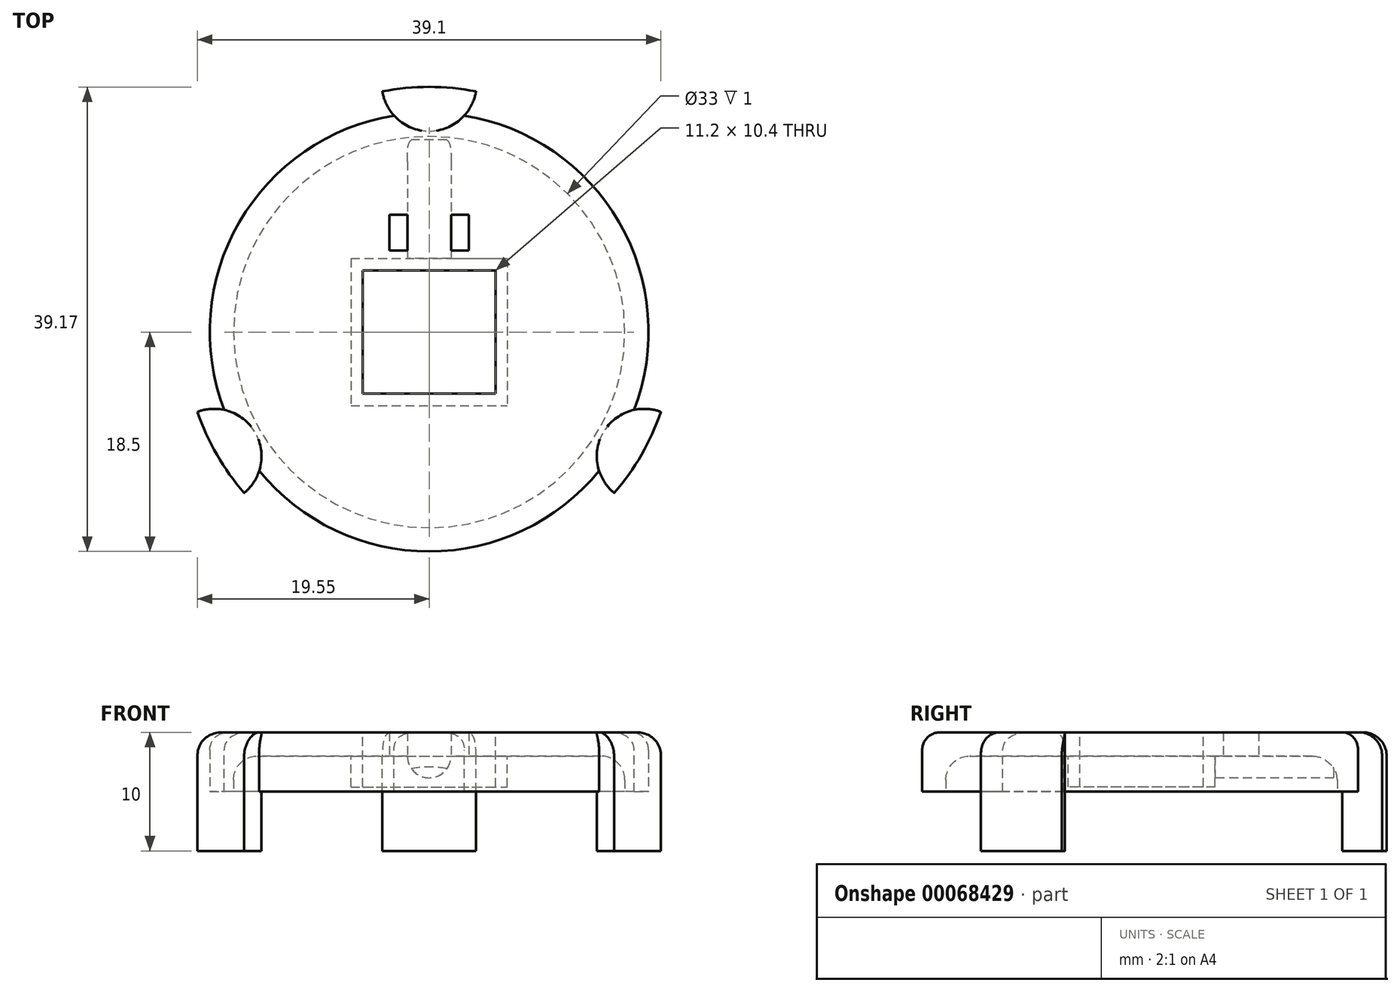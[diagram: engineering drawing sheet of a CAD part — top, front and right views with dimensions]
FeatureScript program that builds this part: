
annotation { "Feature Type Name" : "Feature", "Feature Type Description" : "" }
export const myFeature = defineFeature(function(context is Context, id is Id, definition is map)
    precondition{}
    {
        {
            var Q0;
            Q0=qCreatedBy(makeId("Top.planeOp"),FACE);
            var sketch = newSketch(context, id + "F0", { "sketchPlane" : qUnion([Q0])});
            skCircle(sketch, "E0", {"center": v(0, 0) * mm, "radius": 18.5 * mm});
            skCircle(sketch, "E1", {"center": v(0, 0) * mm, "radius": 20.88 * mm, "construction": true});
            skCircle(sketch, "E2", {"center": v(0, 0) * mm, "radius": 19.1 * mm, "construction": true});
            skCircle(sketch, "E3", {"center": v(-20.88, 0) * mm, "radius": 3.64 * mm});
            skCircle(sketch, "E4", {"center": v(10.44, 18.09) * mm, "radius": 3.64 * mm});
            skCircle(sketch, "E5", {"center": v(10.44, -18.09) * mm, "radius": 3.64 * mm});
            skLineSegment(sketch, "E6", {"start": v(-20.88, 0) * mm, "end": v(0, 0) * mm, "construction": true});
            skLineSegment(sketch, "E7", {"start": v(0, 0) * mm, "end": v(10.44, -18.09) * mm, "construction": true});
            skLineSegment(sketch, "E8", {"start": v(0, 0) * mm, "end": v(10.44, 18.09) * mm, "construction": true});
            skSolve(sketch);
        }
        {
            var Q0;
            {var subQ0=sQuery(id+"F0.wireOp",EDGE,"E4");var subQ1=sQuery(id+"F0.wireOp",EDGE,"E0");var subQ2=makeQuery(id+"F0.imprint","INTERSECT",VERTEX,{"disambiguationData":[OD(0.0)],"derivedFrom":[subQ1,subQ0]});Q0=makeQuery(id+"F0.imprint","IMPRINT",FACE,{"disambiguationData":[TD([[makeQuery(id+"F0.imprint","IMPRINT",EDGE,{"disambiguationData":[TD([[subQ2,1.0]])],"derivedFrom":subQ1}),1.0]])]});}
            var Q1;
            {var subQ0=sQuery(id+"F0.wireOp",EDGE,"E3");var subQ1=sQuery(id+"F0.wireOp",EDGE,"E0");var subQ2=makeQuery(id+"F0.imprint","INTERSECT",VERTEX,{"disambiguationData":[OD(0.0)],"derivedFrom":[subQ1,subQ0]});Q1=makeQuery(id+"F0.imprint","IMPRINT",FACE,{"disambiguationData":[TD([[makeQuery(id+"F0.imprint","IMPRINT",EDGE,{"disambiguationData":[TD([[subQ2,-1.0]])],"derivedFrom":subQ1}),1.0]])]});}
            var Q2;
            {var subQ0=sQuery(id+"F0.wireOp",EDGE,"E5");var subQ1=sQuery(id+"F0.wireOp",EDGE,"E0");var subQ2=makeQuery(id+"F0.imprint","INTERSECT",VERTEX,{"disambiguationData":[OD(0.0)],"derivedFrom":[subQ1,subQ0]});Q2=makeQuery(id+"F0.imprint","IMPRINT",FACE,{"disambiguationData":[TD([[makeQuery(id+"F0.imprint","IMPRINT",EDGE,{"disambiguationData":[TD([[subQ2,-1.0]])],"derivedFrom":subQ1}),1.0]])]});}
            var Q3;
            {var subQ1=sQuery(id+"F0.wireOp",EDGE,"E0");var subQ4=sQuery(id+"F0.wireOp",EDGE,"E4");var subQ9=makeQuery(id+"F0.imprint","INTERSECT",VERTEX,{"disambiguationData":[OD(0.0)],"derivedFrom":[subQ1,subQ4]});Q3=makeQuery(id+"F0.imprint","IMPRINT",FACE,{"disambiguationData":[TD([[makeQuery(id+"F0.imprint","IMPRINT",EDGE,{"disambiguationData":[TD([[subQ9,-1.0]])],"derivedFrom":subQ1}),1.0]])]});}
            extrude(context, id + "F1", {"entities" : qUnion([Q0, Q1, Q2, Q3]), "depth" : 5 * mm});
        }
        {
            var Q0;
            Q0=makeQuery(id+"F1.opExtrude","CAP_FACE",FACE,{"disambiguationData":[OSD([sQuery(id+"F0.wireOp",EDGE,"E0")])],"isStart":true});
            var Q1;
            Q1=makeQuery(id+"F1.opExtrude","SWEPT_BODY",BODY,{"disambiguationData":[OSD([sQuery(id+"F0.wireOp",EDGE,"E0")])]});
            shell(context, id + "F2", {"entities" : qUnion([Q0]), "parts" : qUnion([Q1]), "thickness" : 2 * mm});
        }
        {
            var Q0;
            {var subQ0=sQuery(id+"F0.wireOp",EDGE,"E0");Q0=makeQuery(id+"F2.opShell","OFFSET_EDGE",EDGE,{"disambiguationData":[OSD([subQ0]),TDD([makeQuery(id+"F1.opExtrude","CAP_EDGE",EDGE,{"disambiguationData":[OSD([subQ0])],"isStart":false})])]});}
            fillet(context, id + "F3", {"entities" : qUnion([Q0]), "radius" : 2 * mm, "tangentPropagation" : true, "allowEdgeOverflow" : false});
        }
        {
            var Q0;
            Q0=makeQuery(id+"F1.opExtrude","CAP_FACE",FACE,{"disambiguationData":[OSD([sQuery(id+"F0.wireOp",EDGE,"E0")])],"isStart":false});
            var sketch = newSketch(context, id + "F4", { "sketchPlane" : qUnion([Q0])});
            skLineSegment(sketch, "E9.rect.bottom", {"start": v(-5.6, 5.2) * mm, "end": v(5.6, 5.2) * mm});
            skLineSegment(sketch, "E9.rect.top", {"start": v(-5.6, -5.2) * mm, "end": v(5.6, -5.2) * mm});
            skLineSegment(sketch, "E9.rect.left", {"start": v(-5.6, 5.2) * mm, "end": v(-5.6, -5.2) * mm});
            skLineSegment(sketch, "E9.rect.right", {"start": v(5.6, 5.2) * mm, "end": v(5.6, -5.2) * mm});
            skPoint(sketch, "E9.rect.middle", {"position": v(0, 0) * mm});
            skLineSegment(sketch, "E10.0", {"start": v(-6.6, 6.2) * mm, "end": v(-6.6, -6.2) * mm});
            skLineSegment(sketch, "E10.1", {"start": v(-6.6, 6.2) * mm, "end": v(6.6, 6.2) * mm});
            skLineSegment(sketch, "E10.2", {"start": v(6.6, 6.2) * mm, "end": v(6.6, -6.2) * mm});
            skLineSegment(sketch, "E10.3", {"start": v(-6.6, -6.2) * mm, "end": v(6.6, -6.2) * mm});
            skSolve(sketch);
        }
        {
            var Q0;
            Q0=makeQuery(id+"F4.imprint","IMPRINT",FACE,{"disambiguationData":[TD([[makeQuery(id+"F4.imprint","IMPRINT",EDGE,{"derivedFrom":sQuery(id+"F4.wireOp",EDGE,"E9.rect.bottom")}),-1.0]])]});
            extrude(context, id + "F5", {"entities" : qUnion([Q0]), "operationType" : NewBodyOperationType.REMOVE, "oppositeDirection" : true, "depth" : 25 * mm});
        }
        {
            var Q0;
            Q0=makeQuery(id+"F4.imprint","IMPRINT",FACE,{"disambiguationData":[TD([[makeQuery(id+"F4.imprint","IMPRINT",EDGE,{"derivedFrom":sQuery(id+"F4.wireOp",EDGE,"E9.rect.bottom")}),1.0]])]});
            extrude(context, id + "F6", {"entities" : qUnion([Q0]), "operationType" : NewBodyOperationType.ADD, "oppositeDirection" : true, "depth" : 4.6 * mm});
        }
        {
            var Q0;
            Q0=makeQuery(id+"F6.opExtrude","SWEPT_FACE",FACE,{"disambiguationData":[OSD([sQuery(id+"F4.wireOp",EDGE,"E10.1")])]});
            var sketch = newSketch(context, id + "F7", { "sketchPlane" : qUnion([Q0])});
            skArc(sketch, "E11", {"start": v(-1.84, 3) * mm, "mid": v(0, 1.16) * mm, "end": v(1.84, 3) * mm});
            skSolve(sketch);
        }
        {
            var Q0;
            {var subQ0=sQuery(id+"F7.wireOp",EDGE,"E11");Q0=makeQuery(id+"F7.imprint","IMPRINT",FACE,{"disambiguationData":[TD([[makeQuery(id+"F7.imprint","IMPRINT",EDGE,{"derivedFrom":subQ0}),1.0]])]});}
            extrude(context, id + "F8", {"entities" : qUnion([Q0]), "operationType" : NewBodyOperationType.ADD, "depth" : 10 * mm});
        }
        {
            var Q0;
            {var subQ0=sQuery(id+"F0.wireOp",EDGE,"E0");Q0=makeQuery(id+"F2.opShell","OFFSET_FACE",FACE,{"disambiguationData":[OSD([subQ0]),TDD([makeQuery(id+"F1.opExtrude","CAP_FACE",FACE,{"disambiguationData":[OSD([subQ0])],"isStart":false})])]});}
            var sketch = newSketch(context, id + "F9", { "sketchPlane" : qUnion([Q0])});
            skLineSegment(sketch, "E12.bottom", {"start": v(-1.84, -9.89) * mm, "end": v(-3.34, -9.89) * mm});
            skLineSegment(sketch, "E12.top", {"start": v(-1.84, -6.89) * mm, "end": v(-3.34, -6.89) * mm});
            skLineSegment(sketch, "E12.left", {"start": v(-1.84, -9.89) * mm, "end": v(-1.84, -6.89) * mm});
            skLineSegment(sketch, "E12.right", {"start": v(-3.34, -9.89) * mm, "end": v(-3.34, -6.89) * mm});
            skLineSegment(sketch, "E13.bottom", {"start": v(1.84, -6.89) * mm, "end": v(3.34, -6.89) * mm});
            skLineSegment(sketch, "E13.top", {"start": v(1.84, -9.89) * mm, "end": v(3.34, -9.89) * mm});
            skLineSegment(sketch, "E13.left", {"start": v(1.84, -6.89) * mm, "end": v(1.84, -9.89) * mm});
            skLineSegment(sketch, "E13.right", {"start": v(3.34, -6.89) * mm, "end": v(3.34, -9.89) * mm});
            skSolve(sketch);
        }
        {
            var Q0;
            Q0=qSketchRegion(id+"F9",true);
            extrude(context, id + "F10", {"entities" : qUnion([Q0]), "operationType" : NewBodyOperationType.REMOVE, "oppositeDirection" : true, "depth" : 25 * mm});
        }
        {
            var Q0;
            Q0=makeQuery(id+"F1.opExtrude","CAP_FACE",FACE,{"disambiguationData":[OSD([sQuery(id+"F0.wireOp",EDGE,"E0")])],"isStart":false});
            var sketch = newSketch(context, id + "F11", { "sketchPlane" : qUnion([Q0])});
            skCircle(sketch, "E14", {"center": v(0, 0) * mm, "radius": 18.5 * mm});
            skCircle(sketch, "E15", {"center": v(0, 0) * mm, "radius": 20.94 * mm, "construction": true});
            skCircle(sketch, "E16", {"center": v(0, 0) * mm, "radius": 19.1 * mm, "construction": true});
            skCircle(sketch, "E17", {"center": v(-18.14, -10.47) * mm, "radius": 4 * mm});
            skCircle(sketch, "E18", {"center": v(0, 20.94) * mm, "radius": 4 * mm});
            skCircle(sketch, "E19", {"center": v(18.14, -10.47) * mm, "radius": 4 * mm});
            skLineSegment(sketch, "E20", {"start": v(-18.14, -10.47) * mm, "end": v(0, 0) * mm, "construction": true});
            skLineSegment(sketch, "E21", {"start": v(0, 0) * mm, "end": v(18.14, -10.47) * mm, "construction": true});
            skLineSegment(sketch, "E22", {"start": v(0, 0) * mm, "end": v(0, 20.94) * mm, "construction": true});
            skCircle(sketch, "E23", {"center": v(0, 0) * mm, "radius": 20.67 * mm});
            skSolve(sketch);
        }
        {
            var Q0;
            {var subQ0=sQuery(id+"F11.wireOp",EDGE,"E17");var subQ1=sQuery(id+"F11.wireOp",EDGE,"E14");var subQ2=makeQuery(id+"F11.imprint","INTERSECT",VERTEX,{"disambiguationData":[OD(0.0)],"derivedFrom":[subQ1,subQ0]});Q0=makeQuery(id+"F11.imprint","IMPRINT",FACE,{"disambiguationData":[TD([[makeQuery(id+"F11.imprint","IMPRINT",EDGE,{"disambiguationData":[TD([[subQ2,-1.0]])],"derivedFrom":subQ1}),-1.0]])]});}
            var Q1;
            {var subQ0=sQuery(id+"F11.wireOp",EDGE,"E17");var subQ1=sQuery(id+"F11.wireOp",EDGE,"E14");var subQ2=makeQuery(id+"F11.imprint","INTERSECT",VERTEX,{"disambiguationData":[OD(0.0)],"derivedFrom":[subQ1,subQ0]});Q1=makeQuery(id+"F11.imprint","IMPRINT",FACE,{"disambiguationData":[TD([[makeQuery(id+"F11.imprint","IMPRINT",EDGE,{"disambiguationData":[TD([[subQ2,-1.0]])],"derivedFrom":subQ1}),1.0]])]});}
            var Q2;
            {var subQ0=sQuery(id+"F11.wireOp",EDGE,"E18");var subQ1=sQuery(id+"F11.wireOp",EDGE,"E14");var subQ2=makeQuery(id+"F11.imprint","INTERSECT",VERTEX,{"disambiguationData":[OD(0.0)],"derivedFrom":[subQ1,subQ0]});Q2=makeQuery(id+"F11.imprint","IMPRINT",FACE,{"disambiguationData":[TD([[makeQuery(id+"F11.imprint","IMPRINT",EDGE,{"disambiguationData":[TD([[subQ2,1.0]])],"derivedFrom":subQ1}),1.0]])]});}
            var Q3;
            {var subQ0=sQuery(id+"F11.wireOp",EDGE,"E18");var subQ1=sQuery(id+"F11.wireOp",EDGE,"E14");var subQ2=makeQuery(id+"F11.imprint","INTERSECT",VERTEX,{"disambiguationData":[OD(0.0)],"derivedFrom":[subQ1,subQ0]});Q3=makeQuery(id+"F11.imprint","IMPRINT",FACE,{"disambiguationData":[TD([[makeQuery(id+"F11.imprint","IMPRINT",EDGE,{"disambiguationData":[TD([[subQ2,1.0]])],"derivedFrom":subQ1}),-1.0]])]});}
            var Q4;
            {var subQ0=sQuery(id+"F11.wireOp",EDGE,"E19");var subQ1=sQuery(id+"F11.wireOp",EDGE,"E14");var subQ2=makeQuery(id+"F11.imprint","INTERSECT",VERTEX,{"disambiguationData":[OD(0.0)],"derivedFrom":[subQ1,subQ0]});Q4=makeQuery(id+"F11.imprint","IMPRINT",FACE,{"disambiguationData":[TD([[makeQuery(id+"F11.imprint","IMPRINT",EDGE,{"disambiguationData":[TD([[subQ2,-1.0]])],"derivedFrom":subQ1}),1.0]])]});}
            var Q5;
            {var subQ0=sQuery(id+"F11.wireOp",EDGE,"E19");var subQ1=sQuery(id+"F11.wireOp",EDGE,"E14");var subQ2=makeQuery(id+"F11.imprint","INTERSECT",VERTEX,{"disambiguationData":[OD(0.0)],"derivedFrom":[subQ1,subQ0]});Q5=makeQuery(id+"F11.imprint","IMPRINT",FACE,{"disambiguationData":[TD([[makeQuery(id+"F11.imprint","IMPRINT",EDGE,{"disambiguationData":[TD([[subQ2,-1.0]])],"derivedFrom":subQ1}),-1.0]])]});}
            extrude(context, id + "F12", {"entities" : qUnion([Q0, Q1, Q2, Q3, Q4, Q5]), "operationType" : NewBodyOperationType.ADD, "oppositeDirection" : true, "depth" : 10 * mm});
        }
        {
            var Q0;
            {var subQ0=sQuery(id+"F11.wireOp",EDGE,"E23");var subQ1=sQuery(id+"F11.wireOp",EDGE,"E18");Q0=makeQuery(id+"F12.opExtrude","CAP_EDGE",EDGE,{"disambiguationData":[OSD([subQ0]),TDD([makeQuery(id+"F11.imprint","IMPRINT",EDGE,{"disambiguationData":[TD([[makeQuery(id+"F11.imprint","INTERSECT",VERTEX,{"disambiguationData":[OD(0.0)],"derivedFrom":[subQ1,subQ0]}),1.0]])],"derivedFrom":subQ0})])],"isStart":true});}
            var Q1;
            {var subQ0=sQuery(id+"F11.wireOp",EDGE,"E23");var subQ1=sQuery(id+"F11.wireOp",EDGE,"E19");Q1=makeQuery(id+"F12.opExtrude","CAP_EDGE",EDGE,{"disambiguationData":[OSD([subQ0]),TDD([makeQuery(id+"F11.imprint","IMPRINT",EDGE,{"disambiguationData":[TD([[makeQuery(id+"F11.imprint","INTERSECT",VERTEX,{"disambiguationData":[OD(0.0)],"derivedFrom":[subQ1,subQ0]}),1.0]])],"derivedFrom":subQ0})])],"isStart":true});}
            var Q2;
            {var subQ0=sQuery(id+"F11.wireOp",EDGE,"E23");var subQ1=sQuery(id+"F11.wireOp",EDGE,"E17");Q2=makeQuery(id+"F12.opExtrude","CAP_EDGE",EDGE,{"disambiguationData":[OSD([subQ0]),TDD([makeQuery(id+"F11.imprint","IMPRINT",EDGE,{"disambiguationData":[TD([[makeQuery(id+"F11.imprint","INTERSECT",VERTEX,{"disambiguationData":[OD(0.0)],"derivedFrom":[subQ1,subQ0]}),-1.0]])],"derivedFrom":subQ0})])],"isStart":true});}
            fillet(context, id + "F13", {"entities" : qUnion([Q0, Q1, Q2]), "radius" : 2 * mm, "tangentPropagation" : true, "allowEdgeOverflow" : false});
        }
        {
            var Q0;
            {var subQ0=sQuery(id+"F0.wireOp",EDGE,"E0");var subQ1=sQuery(id+"F11.wireOp",EDGE,"E18");var subQ2=sQuery(id+"F11.wireOp",EDGE,"E19");var subQ3=sQuery(id+"F11.wireOp",EDGE,"E23");Q0=makeQuery(id+"F12.boolean.opBoolean","SPLIT",EDGE,{"disambiguationData":[TD([makeQuery(id+"F1.opExtrude","SWEPT_FACE",FACE,{"disambiguationData":[OSD([subQ0])]}),makeQuery(id+"F1.opExtrude","CAP_FACE",FACE,{"disambiguationData":[OSD([subQ0])],"isStart":false}),makeQuery(id+"F12.opExtrude","CAP_FACE",FACE,{"disambiguationData":[OSD([sQuery(id+"F11.wireOp",EDGE,"E17"),subQ3])],"isStart":true}),makeQuery(id+"F12.opExtrude","SWEPT_FACE",FACE,{"disambiguationData":[OSD([subQ1])]}),makeQuery(id+"F12.opExtrude","CAP_FACE",FACE,{"disambiguationData":[OSD([subQ1,subQ3])],"isStart":true}),makeQuery(id+"F12.opExtrude","SWEPT_FACE",FACE,{"disambiguationData":[OSD([subQ2])]}),makeQuery(id+"F12.opExtrude","CAP_FACE",FACE,{"disambiguationData":[OSD([subQ2,subQ3])],"isStart":true})])],"derivedFrom":makeQuery(id+"F1.opExtrude","CAP_EDGE",EDGE,{"disambiguationData":[OSD([subQ0])],"isStart":false})});}
            var Q1;
            {var subQ0=sQuery(id+"F11.wireOp",EDGE,"E17");var subQ1=sQuery(id+"F0.wireOp",EDGE,"E0");var subQ2=sQuery(id+"F11.wireOp",EDGE,"E23");var subQ3=sQuery(id+"F11.wireOp",EDGE,"E19");Q1=makeQuery(id+"F12.boolean.opBoolean","SPLIT",EDGE,{"disambiguationData":[TD([makeQuery(id+"F1.opExtrude","SWEPT_FACE",FACE,{"disambiguationData":[OSD([subQ1])]}),makeQuery(id+"F1.opExtrude","CAP_FACE",FACE,{"disambiguationData":[OSD([subQ1])],"isStart":false}),makeQuery(id+"F12.opExtrude","SWEPT_FACE",FACE,{"disambiguationData":[OSD([subQ0])]}),makeQuery(id+"F12.opExtrude","CAP_FACE",FACE,{"disambiguationData":[OSD([subQ0,subQ2])],"isStart":true}),makeQuery(id+"F12.opExtrude","CAP_FACE",FACE,{"disambiguationData":[OSD([sQuery(id+"F11.wireOp",EDGE,"E18"),subQ2])],"isStart":true}),makeQuery(id+"F12.opExtrude","SWEPT_FACE",FACE,{"disambiguationData":[OSD([subQ3])]}),makeQuery(id+"F12.opExtrude","CAP_FACE",FACE,{"disambiguationData":[OSD([subQ3,subQ2])],"isStart":true})])],"derivedFrom":makeQuery(id+"F1.opExtrude","CAP_EDGE",EDGE,{"disambiguationData":[OSD([subQ1])],"isStart":false})});}
            var Q2;
            {var subQ0=sQuery(id+"F11.wireOp",EDGE,"E17");var subQ1=sQuery(id+"F0.wireOp",EDGE,"E0");var subQ2=sQuery(id+"F11.wireOp",EDGE,"E23");var subQ3=sQuery(id+"F11.wireOp",EDGE,"E18");Q2=makeQuery(id+"F12.boolean.opBoolean","SPLIT",EDGE,{"disambiguationData":[TD([makeQuery(id+"F1.opExtrude","SWEPT_FACE",FACE,{"disambiguationData":[OSD([subQ1])]}),makeQuery(id+"F1.opExtrude","CAP_FACE",FACE,{"disambiguationData":[OSD([subQ1])],"isStart":false}),makeQuery(id+"F12.opExtrude","SWEPT_FACE",FACE,{"disambiguationData":[OSD([subQ0])]}),makeQuery(id+"F12.opExtrude","CAP_FACE",FACE,{"disambiguationData":[OSD([subQ0,subQ2])],"isStart":true}),makeQuery(id+"F12.opExtrude","SWEPT_FACE",FACE,{"disambiguationData":[OSD([subQ3])]}),makeQuery(id+"F12.opExtrude","CAP_FACE",FACE,{"disambiguationData":[OSD([subQ3,subQ2])],"isStart":true}),makeQuery(id+"F12.opExtrude","CAP_FACE",FACE,{"disambiguationData":[OSD([sQuery(id+"F11.wireOp",EDGE,"E19"),subQ2])],"isStart":true})])],"derivedFrom":makeQuery(id+"F1.opExtrude","CAP_EDGE",EDGE,{"disambiguationData":[OSD([subQ1])],"isStart":false})});}
            fillet(context, id + "F14", {"entities" : qUnion([Q0, Q1, Q2]), "radius" : 1.5 * mm, "tangentPropagation" : true, "allowEdgeOverflow" : false});
        }
    });
